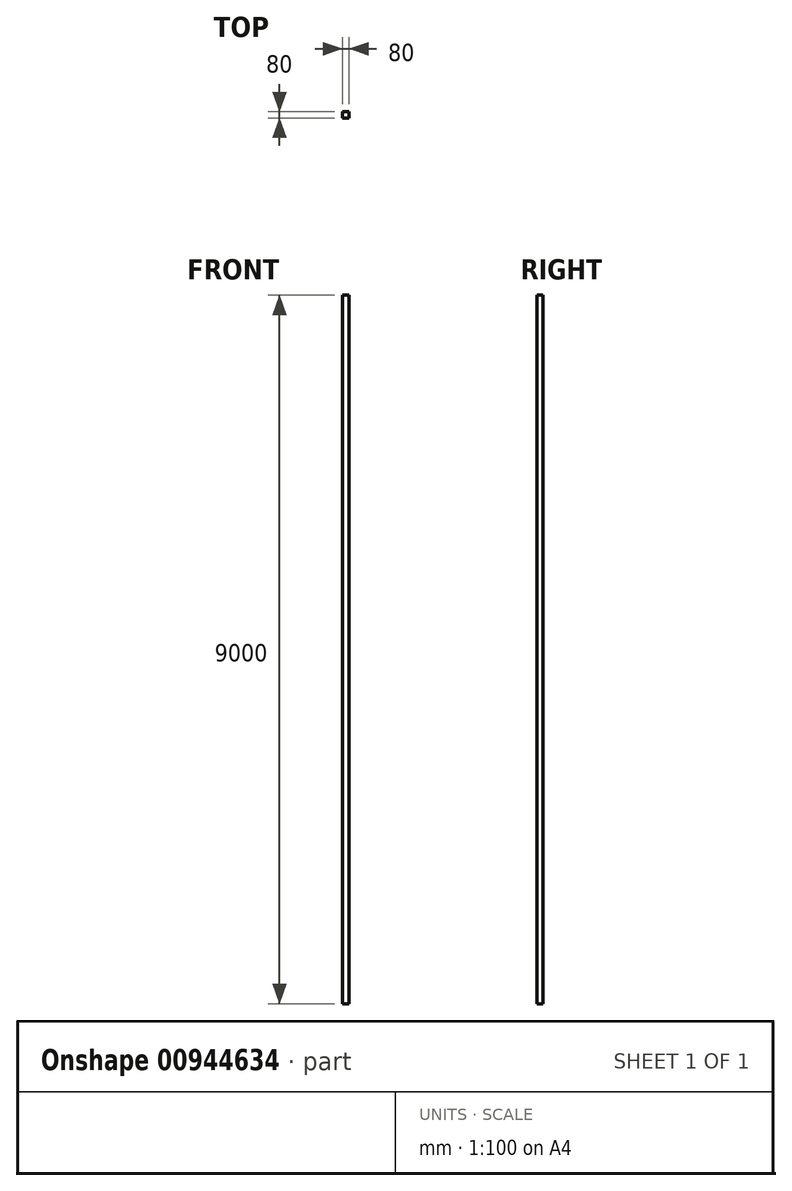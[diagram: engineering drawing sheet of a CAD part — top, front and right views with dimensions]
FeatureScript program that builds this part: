
annotation { "Feature Type Name" : "Feature", "Feature Type Description" : "" }
export const myFeature = defineFeature(function(context is Context, id is Id, definition is map)
    precondition{}
    {
        {
            var Q0;
            Q0=qCreatedBy(makeId("Top.planeOp"),FACE);
            var sketch = newSketch(context, id + "F0", { "sketchPlane" : qUnion([Q0])});
            skLineSegment(sketch, "E0.bottom", {"start": v(0, 0) * mm, "end": v(80, 0) * mm});
            skLineSegment(sketch, "E0.top", {"start": v(0, 80) * mm, "end": v(80, 80) * mm});
            skLineSegment(sketch, "E0.left", {"start": v(0, 0) * mm, "end": v(0, 80) * mm});
            skLineSegment(sketch, "E0.right", {"start": v(80, 0) * mm, "end": v(80, 80) * mm});
            skSolve(sketch);
        }
        {
            var Q0;
            Q0=makeQuery(id+"F0.imprint","IMPRINT",FACE,{"disambiguationData":[TD([[makeQuery(id+"F0.imprint","IMPRINT",EDGE,{"derivedFrom":sQuery(id+"F0.wireOp",EDGE,"E0.bottom")}),1.0]])]});
            extrude(context, id + "F1", {"entities" : qUnion([Q0]), "depth" : 9000 * mm, "offsetDistance" : 25 * mm});
        }
    });
